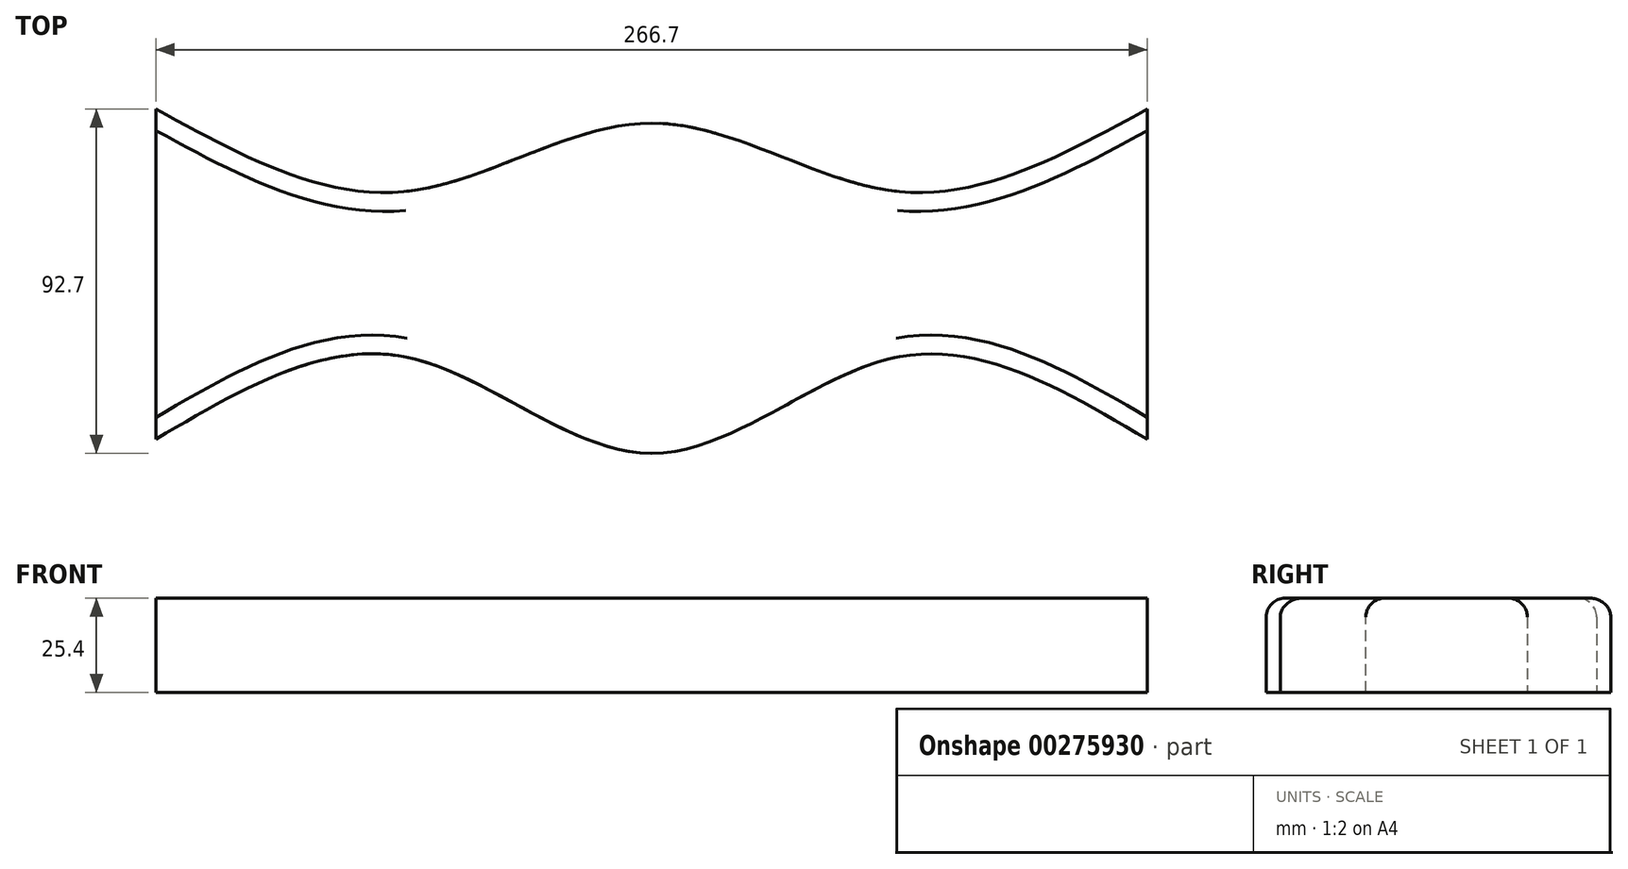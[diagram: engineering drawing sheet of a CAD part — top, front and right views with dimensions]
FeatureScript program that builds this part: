
annotation { "Feature Type Name" : "Feature", "Feature Type Description" : "" }
export const myFeature = defineFeature(function(context is Context, id is Id, definition is map)
    precondition{}
    {
        {
            var Q0;
            Q0=qCreatedBy(makeId("Top.planeOp"),FACE);
            var sketch = newSketch(context, id + "F0", { "sketchPlane" : qUnion([Q0])});
            skLineSegment(sketch, "E0", {"start": v(0, 0) * mm, "end": v(0, 40.65) * mm});
            skLineSegment(sketch, "E1", {"start": v(0, 40.65) * mm, "end": v(0, -48.25) * mm});
            skLineSegment(sketch, "E2", {"start": v(0, 0) * mm, "end": v(-133.35, 0) * mm});
            skLineSegment(sketch, "E3", {"start": v(0, 0) * mm, "end": v(133.35, 0) * mm});
            skLineSegment(sketch, "E4", {"start": v(-133.35, 0) * mm, "end": v(-133.35, 44.45) * mm});
            skLineSegment(sketch, "E5", {"start": v(-133.35, 0) * mm, "end": v(-133.35, -44.45) * mm});
            skLineSegment(sketch, "E6", {"start": v(133.35, 0) * mm, "end": v(133.35, 44.45) * mm});
            skLineSegment(sketch, "E7", {"start": v(133.35, 0) * mm, "end": v(133.35, -44.45) * mm});
            skLineSegment(sketch, "E8", {"start": v(0, 0) * mm, "end": v(-66.68, 0) * mm});
            skLineSegment(sketch, "E9", {"start": v(0, 0) * mm, "end": v(66.68, 0) * mm});
            skLineSegment(sketch, "E10", {"start": v(-66.68, 0) * mm, "end": v(-66.68, 22.22) * mm});
            skLineSegment(sketch, "E11", {"start": v(-66.68, 0) * mm, "end": v(-66.68, -22.23) * mm});
            skLineSegment(sketch, "E12", {"start": v(66.68, 0) * mm, "end": v(66.68, 22.23) * mm});
            skLineSegment(sketch, "E13", {"start": v(66.68, 0) * mm, "end": v(66.68, -22.23) * mm});
            skFitSpline(sketch, "E14", {"points": [v(-133.35, 44.45) * mm, v(-66.68, 22.22) * mm, v(0, 40.65) * mm, v(66.68, 22.23) * mm, v(133.35, 44.45) * mm], "startDerivative": vector(265.11, -145.76) * mm, "endDerivative": vector(265.11, 145.76) * mm});
            skFitSpline(sketch, "E15", {"points": [v(-133.35, -44.45) * mm, v(-66.68, -22.23) * mm, v(0, -48.25) * mm, v(66.68, -22.23) * mm, v(133.35, -44.45) * mm], "startDerivative": vector(268.52, 158.96) * mm, "endDerivative": vector(268.52, -158.96) * mm});
            skSolve(sketch);
        }
        {
            var Q0;
            Q0=qSketchRegion(id+"F0",true);
            extrude(context, id + "F1", {"entities" : qUnion([Q0]), "depth" : 25.4 * mm});
        }
        {
            var Q0;
            Q0=makeQuery(id+"F1.opExtrude","CAP_EDGE",EDGE,{"disambiguationData":[OSD([sQuery(id+"F0.wireOp",EDGE,"E15")])],"isStart":false});
            var Q1;
            Q1=makeQuery(id+"F1.opExtrude","CAP_EDGE",EDGE,{"disambiguationData":[OSD([sQuery(id+"F0.wireOp",EDGE,"E14")])],"isStart":false});
            fillet(context, id + "F2", {"entities" : qUnion([Q0, Q1]), "radius" : 5.08 * mm, "tangentPropagation" : true, "allowEdgeOverflow" : false});
        }
    });
